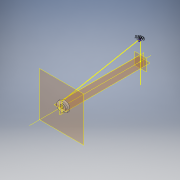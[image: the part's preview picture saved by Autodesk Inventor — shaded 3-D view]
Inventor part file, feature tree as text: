
AUTODESK INVENTOR PART (.ipt)
format: ipt  version: 2018 (Build 220112000, 112)  size: 280,576 bytes
history: native  units: in
note: dims shown in document units (in); Inventor stores cm internally (conversion verified against a paired STEP export)
features: sketch x4, helix x2, plane x1, loft x1, hole x1, other x1, extrude x1, projected_geometry x1
ambient origin geometry x8: Origin, YZ Plane, XZ Plane, XY Plane, X Axis, Y Axis, Z Axis, Center Point
bodies: Solid1 (feature_tree)
feature tree (12):
  sketch  "Sketch1"  dims[d0=2.0in d2=3.9in]
  plane  "Work Plane1"
  loft  "Loft1"
  hole  "Hole1"  [1 undecoded]
  other  "Work Axis2"
  sketch  "Sketch6"  dims[d65=1.0in d66=1.0in d11=0.18in d12=0.75in d13=0.375in d14=0.25in d15=0.5635in d16=1.0in d17=0.8108in d41=0.1in]
  helix  "Coil3"  [1 undecoded]
  helix  "Coil4"  [1 undecoded]
  extrude  "Extrusion2"  Depth=1.0in
  sketch  "Sketch2"  dims[d3=0.5in d5=0.0in d6=90.0deg d7=0.0in d8=90.0deg]
  projected_geometry  "Projected Loop1"
  sketch  "Sketch8"  dims[d42=0.1in d43=0.02in d44=0.195in d45=1.0in d46=7.874in d47=-0.0739in d48=90.0deg d49=90.0deg d50=0.0in d51=0.0in d52=0.195in d53=1.0in d54=7.874in d55=0.0756in d56=90.0deg d57=90.0deg d58=0.0in d59=0.0in d60=3.775in d63=3.0in d64=0.0in]
note: 3 required parameter values undecoded (feature->parameter linkage not recoverable at this tier; creation-order binding heuristic only, values carry confidence <= 0.55)
